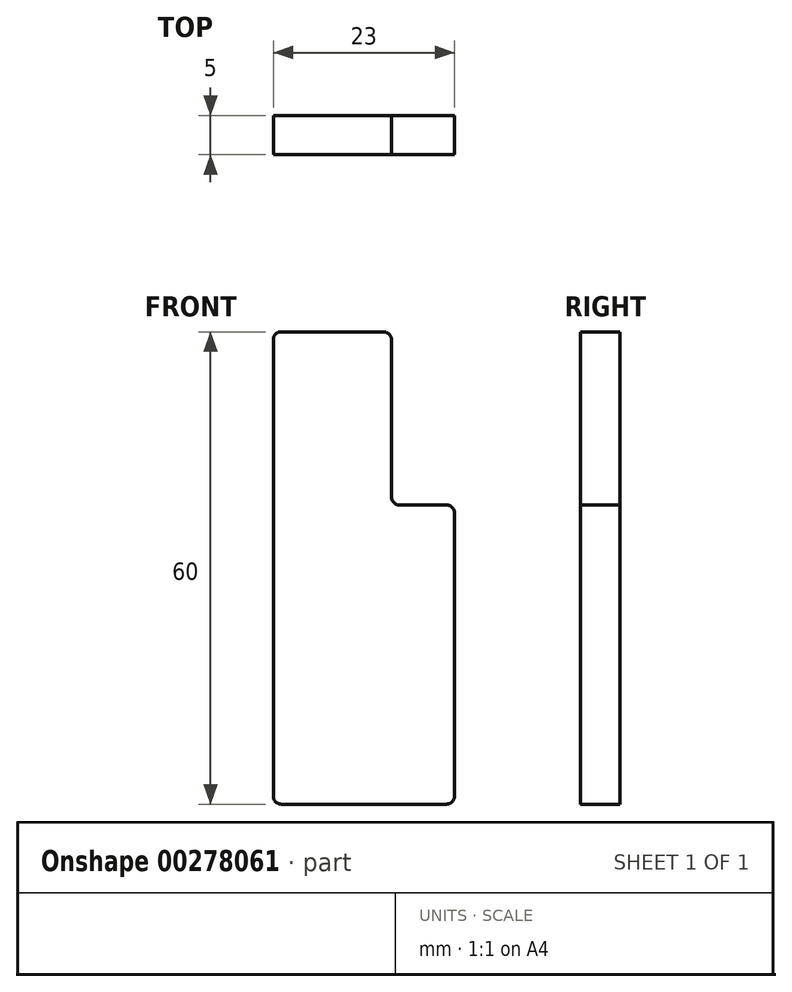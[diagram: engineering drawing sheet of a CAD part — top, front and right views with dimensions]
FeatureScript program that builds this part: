
annotation { "Feature Type Name" : "Feature", "Feature Type Description" : "" }
export const myFeature = defineFeature(function(context is Context, id is Id, definition is map)
    precondition{}
    {
        {
            var Q0;
            Q0=qCreatedBy(makeId("Front.planeOp"),FACE);
            var sketch = newSketch(context, id + "F0", { "sketchPlane" : qUnion([Q0])});
            skLineSegment(sketch, "E0", {"start": v(0, 0) * mm, "end": v(23, 0) * mm});
            skLineSegment(sketch, "E1", {"start": v(23, 0) * mm, "end": v(23, 38) * mm});
            skLineSegment(sketch, "E2", {"start": v(23, 38) * mm, "end": v(15, 38) * mm});
            skLineSegment(sketch, "E3", {"start": v(15, 38) * mm, "end": v(15, 60) * mm});
            skLineSegment(sketch, "E4", {"start": v(15, 60) * mm, "end": v(0, 60) * mm});
            skLineSegment(sketch, "E5", {"start": v(0, 60) * mm, "end": v(0, 0) * mm});
            skSolve(sketch);
        }
        {
            var Q0;
            Q0 = qSketchRegion(id + "F0", true);
            extrude(context, id + "F1", {"entities" : qUnion([Q0]), "depth" : 5 * mm});
        }
        {
            var Q0;
            Q0=makeQuery(id+"F1.opExtrude","SWEPT_EDGE",EDGE,{"disambiguationData":[OSD([sQuery(id+"F0.wireOp",EDGE,"E4"),sQuery(id+"F0.wireOp",EDGE,"E5")])]});
            var Q1;
            Q1=makeQuery(id+"F1.opExtrude","SWEPT_EDGE",EDGE,{"disambiguationData":[OSD([sQuery(id+"F0.wireOp",EDGE,"E3"),sQuery(id+"F0.wireOp",EDGE,"E4")])]});
            var Q2;
            Q2=makeQuery(id+"F1.opExtrude","SWEPT_EDGE",EDGE,{"disambiguationData":[OSD([sQuery(id+"F0.wireOp",EDGE,"E1"),sQuery(id+"F0.wireOp",EDGE,"E2")])]});
            var Q3;
            Q3=makeQuery(id+"F1.opExtrude","SWEPT_EDGE",EDGE,{"disambiguationData":[OSD([sQuery(id+"F0.wireOp",EDGE,"E0"),sQuery(id+"F0.wireOp",EDGE,"E5")])]});
            var Q4;
            Q4=makeQuery(id+"F1.opExtrude","SWEPT_EDGE",EDGE,{"disambiguationData":[OSD([sQuery(id+"F0.wireOp",EDGE,"E0"),sQuery(id+"F0.wireOp",EDGE,"E1")])]});
            fillet(context, id + "F2", {"entities" : qUnion([Q0, Q1, Q2, Q3, Q4]), "radius" : 1 * mm, "tangentPropagation" : true, "allowEdgeOverflow" : false});
        }
        {
            var Q0;
            Q0=makeQuery(id+"F1.opExtrude","SWEPT_EDGE",EDGE,{"disambiguationData":[OSD([sQuery(id+"F0.wireOp",EDGE,"E2"),sQuery(id+"F0.wireOp",EDGE,"E3")])]});
            fillet(context, id + "F3", {"entities" : qUnion([Q0]), "radius" : 1 * mm, "tangentPropagation" : true, "allowEdgeOverflow" : false});
        }
    });
